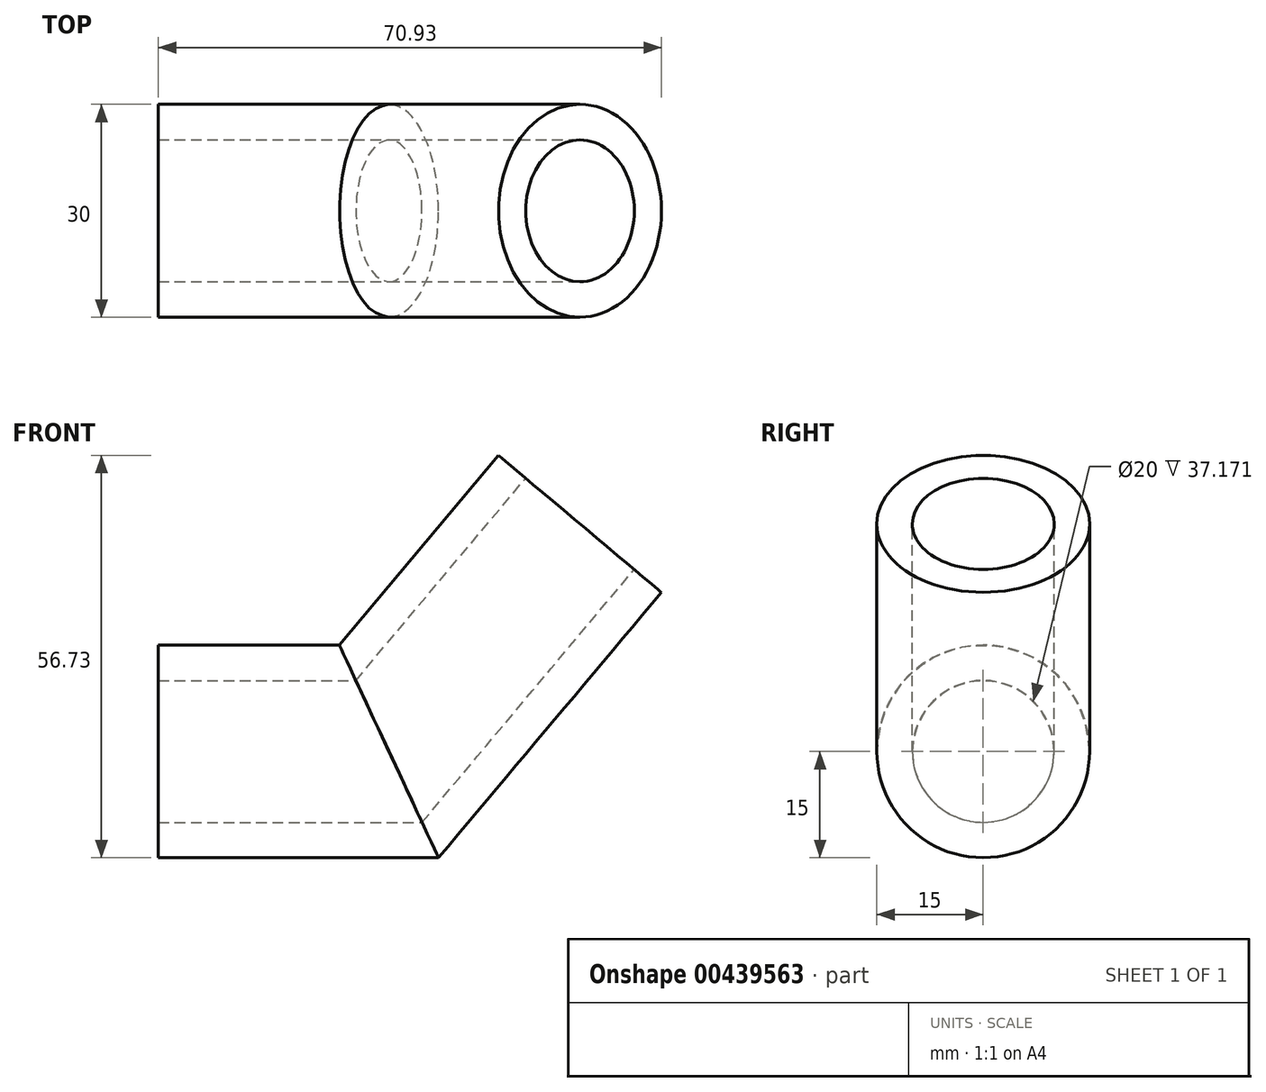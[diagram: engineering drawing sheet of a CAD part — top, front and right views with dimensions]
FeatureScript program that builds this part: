
annotation { "Feature Type Name" : "Feature", "Feature Type Description" : "" }
export const myFeature = defineFeature(function(context is Context, id is Id, definition is map)
    precondition{}
    {
        {
            var Q0;
            Q0=qCreatedBy(makeId("Front.planeOp"),FACE);
            var sketch = newSketch(context, id + "F0", { "sketchPlane" : qUnion([Q0])});
            skLineSegment(sketch, "E0", {"start": v(0, 0) * mm, "end": v(32.5, 0) * mm});
            skLineSegment(sketch, "E1", {"start": v(32.5, 0) * mm, "end": v(59.44, 32.08) * mm});
            skSolve(sketch);
        }
        {
            var Q0;
            Q0=qCreatedBy(makeId("Right.planeOp"),FACE);
            var sketch = newSketch(context, id + "F1", { "sketchPlane" : qUnion([Q0])});
            skCircle(sketch, "E2", {"center": v(0, 0) * mm, "radius": 10 * mm});
            skCircle(sketch, "E3", {"center": v(0, 0) * mm, "radius": 15 * mm});
            skSolve(sketch);
        }
        {
            var Q0;
            Q0=makeQuery(id+"F1.imprint","IMPRINT",FACE,{"disambiguationData":[TD([[makeQuery(id+"F1.imprint","IMPRINT",EDGE,{"derivedFrom":sQuery(id+"F1.wireOp",EDGE,"E2")}),-1.0]])]});
            var Q1;
            Q1=sQuery(id+"F0.wireOp",EDGE,"E0");
            var Q2;
            Q2=sQuery(id+"F0.wireOp",EDGE,"E1");
            sweep(context, id + "F2", {"profiles" : qUnion([Q0]), "path" : qUnion([Q1, Q2])});
        }
    });
